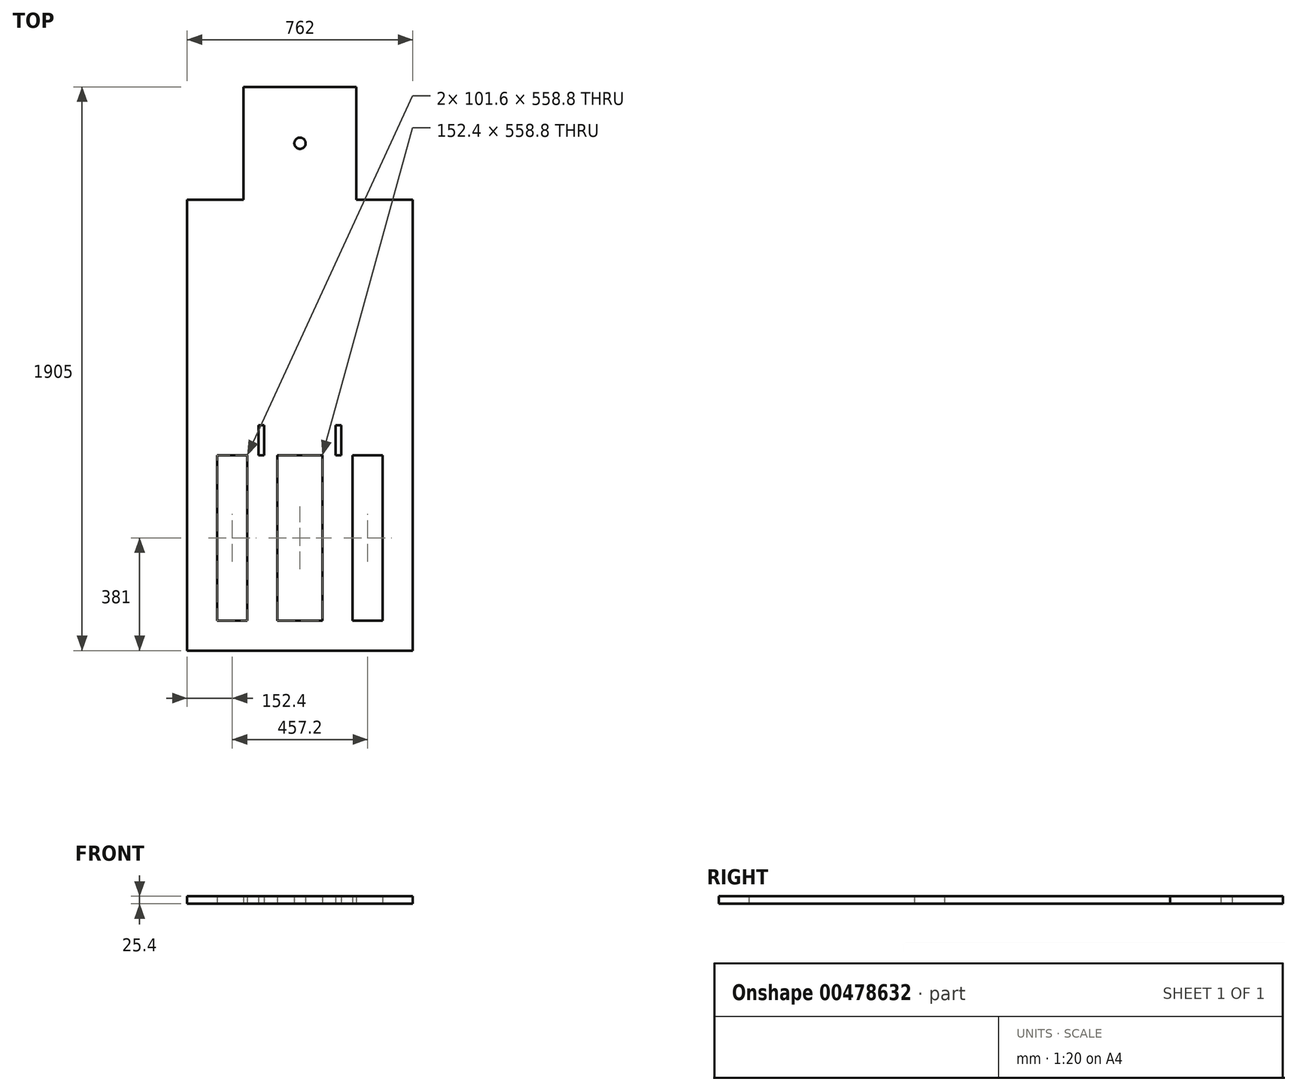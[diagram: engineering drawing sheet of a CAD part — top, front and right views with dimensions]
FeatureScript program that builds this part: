
annotation { "Feature Type Name" : "Feature", "Feature Type Description" : "" }
export const myFeature = defineFeature(function(context is Context, id is Id, definition is map)
    precondition{}
    {
        {
            var Q0;
            Q0=qCreatedBy(makeId("Top.planeOp"),FACE);
            var sketch = newSketch(context, id + "F0", { "sketchPlane" : qUnion([Q0])});
            skLineSegment(sketch, "E0.bottom", {"start": v(381, 762) * mm, "end": v(-381, 762) * mm});
            skLineSegment(sketch, "E0.top", {"start": v(381, -762) * mm, "end": v(-381, -762) * mm});
            skLineSegment(sketch, "E0.left", {"start": v(381, 762) * mm, "end": v(381, -762) * mm});
            skLineSegment(sketch, "E0.right", {"start": v(-381, 762) * mm, "end": v(-381, -762) * mm});
            skPoint(sketch, "E0.middle", {"position": v(0, 0) * mm});
            skLineSegment(sketch, "E1.bottom", {"start": v(-190.5, 1143) * mm, "end": v(190.5, 1143) * mm});
            skLineSegment(sketch, "E1.top", {"start": v(-190.5, 762) * mm, "end": v(190.5, 762) * mm});
            skLineSegment(sketch, "E1.left", {"start": v(-190.5, 1143) * mm, "end": v(-190.5, 762) * mm});
            skLineSegment(sketch, "E1.right", {"start": v(190.5, 1143) * mm, "end": v(190.5, 762) * mm});
            skLineSegment(sketch, "E2", {"start": v(0, 762) * mm, "end": v(381, 762) * mm, "construction": true});
            skLineSegment(sketch, "E3", {"start": v(0, 762) * mm, "end": v(0, -762) * mm, "construction": true});
            skLineSegment(sketch, "E4.bottom", {"start": v(76.2, -101.6) * mm, "end": v(-76.2, -101.6) * mm});
            skLineSegment(sketch, "E4.top", {"start": v(76.2, -660.4) * mm, "end": v(-76.2, -660.4) * mm});
            skLineSegment(sketch, "E4.left", {"start": v(76.2, -101.6) * mm, "end": v(76.2, -660.4) * mm});
            skLineSegment(sketch, "E4.right", {"start": v(-76.2, -101.6) * mm, "end": v(-76.2, -660.4) * mm});
            skPoint(sketch, "E4.middle", {"position": v(0, -381) * mm});
            skLineSegment(sketch, "E5", {"start": v(-381, -381) * mm, "end": v(381, -381) * mm, "construction": true});
            skPoint(sketch, "E5.startSnap0", {"position": v(-76.2, -381) * mm});
            skPoint(sketch, "E5.endSnap0", {"position": v(76.2, -381) * mm});
            skLineSegment(sketch, "E6.bottom", {"start": v(-177.8, -101.6) * mm, "end": v(-279.4, -101.6) * mm});
            skLineSegment(sketch, "E6.top", {"start": v(-177.8, -660.4) * mm, "end": v(-279.4, -660.4) * mm});
            skLineSegment(sketch, "E6.left", {"start": v(-177.8, -101.6) * mm, "end": v(-177.8, -660.4) * mm});
            skLineSegment(sketch, "E6.right", {"start": v(-279.4, -101.6) * mm, "end": v(-279.4, -660.4) * mm});
            skPoint(sketch, "E6.middle", {"position": v(-228.6, -381) * mm});
            skPoint(sketch, "E7.MirrorP", {"position": v(228.6, -381) * mm});
            skLineSegment(sketch, "E8.MirrorCS", {"start": v(177.8, -101.6) * mm, "end": v(177.8, -660.4) * mm});
            skLineSegment(sketch, "E9.MirrorCS", {"start": v(279.4, -101.6) * mm, "end": v(279.4, -660.4) * mm});
            skLineSegment(sketch, "E10.MirrorCS", {"start": v(177.8, -660.4) * mm, "end": v(279.4, -660.4) * mm});
            skLineSegment(sketch, "E11.MirrorCS", {"start": v(177.8, -101.6) * mm, "end": v(279.4, -101.6) * mm});
            skLineSegment(sketch, "E12", {"start": v(0, -50.8) * mm, "end": v(381, -50.8) * mm, "construction": true});
            skPoint(sketch, "E13.cornerSnap0", {"position": v(190.5, -50.8) * mm});
            skLineSegment(sketch, "E14.bottom", {"start": v(139.45, 0) * mm, "end": v(120.9, 0) * mm});
            skLineSegment(sketch, "E14.top", {"start": v(139.45, -101.6) * mm, "end": v(120.9, -101.6) * mm});
            skLineSegment(sketch, "E14.left", {"start": v(139.45, 0) * mm, "end": v(139.45, -101.6) * mm});
            skLineSegment(sketch, "E14.right", {"start": v(120.9, 0) * mm, "end": v(120.9, -101.6) * mm});
            skPoint(sketch, "E14.middle", {"position": v(130.18, -50.8) * mm});
            skLineSegment(sketch, "E15.MirrorCS", {"start": v(-139.45, 0) * mm, "end": v(-120.9, 0) * mm});
            skLineSegment(sketch, "E16.MirrorCS", {"start": v(-139.45, -101.6) * mm, "end": v(-120.9, -101.6) * mm});
            skLineSegment(sketch, "E17.MirrorCS", {"start": v(-139.45, 0) * mm, "end": v(-139.45, -101.6) * mm});
            skLineSegment(sketch, "E18.MirrorCS", {"start": v(-120.9, 0) * mm, "end": v(-120.9, -101.6) * mm});
            skPoint(sketch, "E19.MirrorP", {"position": v(-130.18, -50.8) * mm});
            skLineSegment(sketch, "E20", {"start": v(0, 1143) * mm, "end": v(0, 762) * mm, "construction": true});
            skCircle(sketch, "E21", {"center": v(0, 952.5) * mm, "radius": 19.05 * mm});
            skSolve(sketch);
        }
        {
            var Q0;
            Q0=makeQuery(id+"F0.imprint","IMPRINT",FACE,{"disambiguationData":[TD([[makeQuery(id+"F0.imprint","IMPRINT",EDGE,{"derivedFrom":sQuery(id+"F0.wireOp",EDGE,"E0.top")}),-1.0]])]});
            var Q1;
            Q1=makeQuery(id+"F0.imprint","IMPRINT",FACE,{"disambiguationData":[TD([[makeQuery(id+"F0.imprint","IMPRINT",EDGE,{"derivedFrom":sQuery(id+"F0.wireOp",EDGE,"E1.bottom")}),-1.0]])]});
            extrude(context, id + "F1", {"entities" : qUnion([Q0, Q1]), "depth" : 25.4 * mm, "offsetDistance" : 25.4 * mm});
        }
    });
